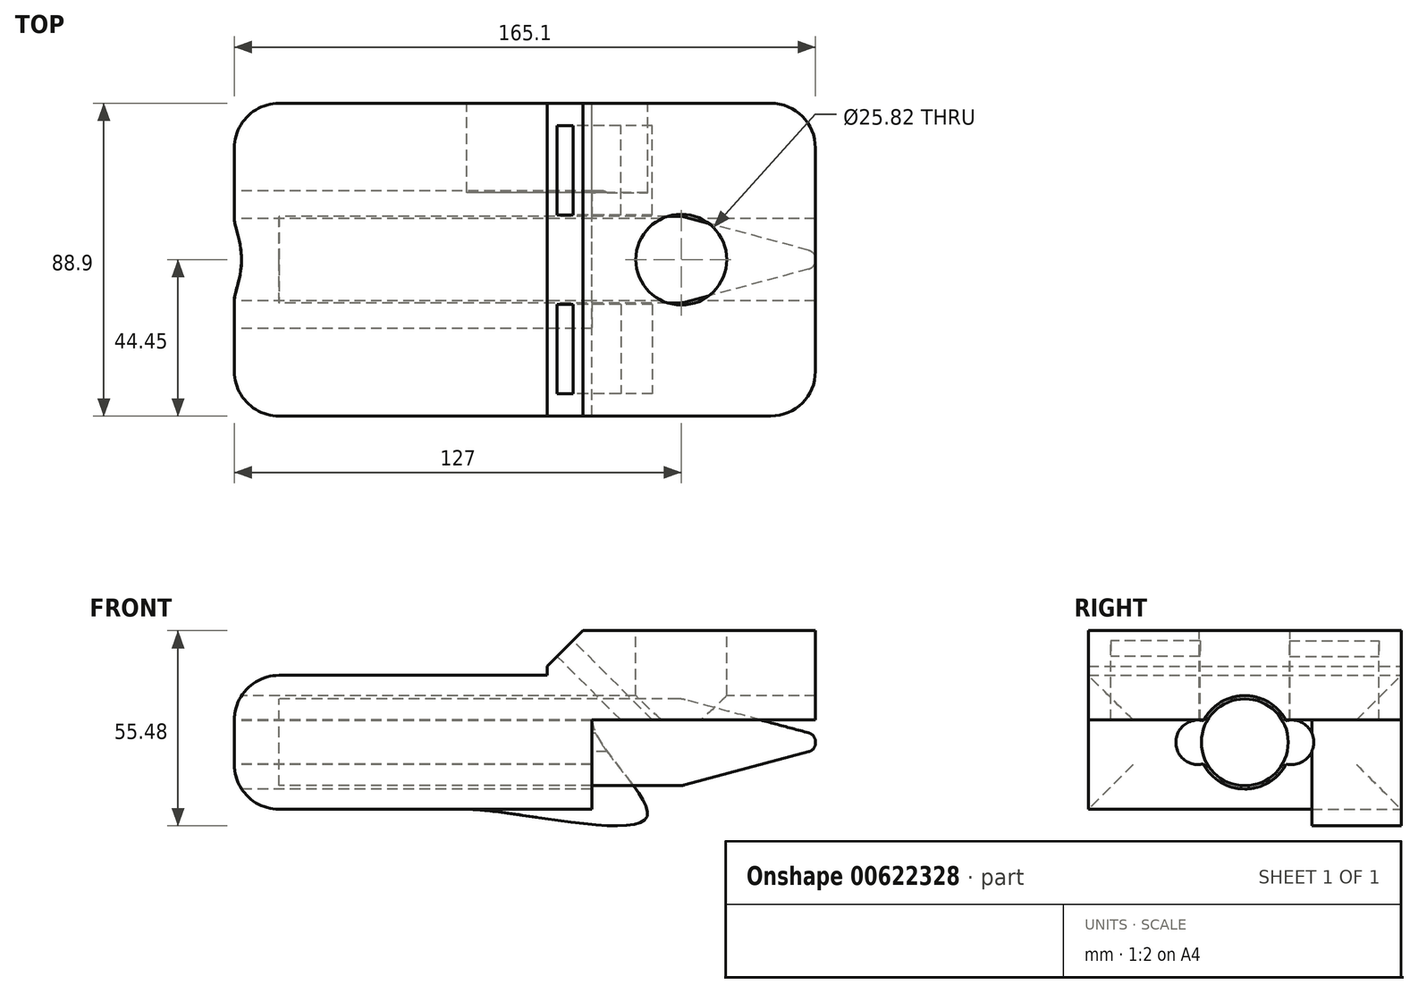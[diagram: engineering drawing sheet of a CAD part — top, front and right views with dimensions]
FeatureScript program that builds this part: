
annotation { "Feature Type Name" : "Feature", "Feature Type Description" : "" }
export const myFeature = defineFeature(function(context is Context, id is Id, definition is map)
    precondition{}
    {
        {
            var Q0;
            Q0=qCreatedBy(makeId("Front.planeOp"),FACE);
            var sketch = newSketch(context, id + "F0", { "sketchPlane" : qUnion([Q0])});
            skLineSegment(sketch, "E0.bottom", {"start": v(50.8, 19.05) * mm, "end": v(-50.8, 19.05) * mm});
            skLineSegment(sketch, "E0.top", {"start": v(50.8, -19.05) * mm, "end": v(-50.8, -19.05) * mm});
            skLineSegment(sketch, "E0.left", {"start": v(50.8, 19.05) * mm, "end": v(50.8, -19.05) * mm});
            skLineSegment(sketch, "E0.right", {"start": v(-50.8, 19.05) * mm, "end": v(-50.8, -19.05) * mm});
            skPoint(sketch, "E0.middle", {"position": v(0, 0) * mm});
            skLineSegment(sketch, "E1.bottom", {"start": v(38.1, 6.35) * mm, "end": v(114.3, 6.35) * mm});
            skLineSegment(sketch, "E1.top", {"start": v(38.1, 31.75) * mm, "end": v(114.3, 31.75) * mm});
            skLineSegment(sketch, "E1.left", {"start": v(38.1, 6.35) * mm, "end": v(38.1, 31.75) * mm});
            skLineSegment(sketch, "E1.right", {"start": v(114.3, 6.35) * mm, "end": v(114.3, 31.75) * mm});
            skPoint(sketch, "E1.middle", {"position": v(76.2, 19.05) * mm});
            skSolve(sketch);
        }
        {
            var Q0;
            Q0 = qSketchRegion(id + "F0", true);
            extrude(context, id + "F1", {"entities" : qUnion([Q0]), "depth" : 88.9 * mm, "offsetDistance" : 25.4 * mm});
        }
        {
            var Q0;
            Q0=makeQuery(id+"F1.opExtrude","SWEPT_FACE",FACE,{"disambiguationData":[OSD([sQuery(id+"F0.wireOp",EDGE,"E1.top")])]});
            var sketch = newSketch(context, id + "F2", { "sketchPlane" : qUnion([Q0])});
            skCircle(sketch, "E2", {"center": v(76.2, -44.45) * mm, "radius": 12.9 * mm});
            skPoint(sketch, "E2.centerSnap0", {"position": v(38.1, -44.45) * mm});
            skPoint(sketch, "E2.centerSnap1", {"position": v(76.2, -88.9) * mm});
            skSolve(sketch);
        }
        {
            var Q0;
            Q0 = qSketchRegion(id + "F2", true);
            extrude(context, id + "F3", {"entities" : qUnion([Q0]), "operationType" : NewBodyOperationType.REMOVE, "oppositeDirection" : true, "depth" : 25.4 * mm, "offsetDistance" : 25.4 * mm});
        }
        {
            var Q0;
            Q0=makeQuery(id+"F1.opExtrude","CAP_EDGE",EDGE,{"disambiguationData":[OSD([sQuery(id+"F0.wireOp",EDGE,"E1.right")])],"isStart":false});
            var Q1;
            Q1=makeQuery(id+"F1.opExtrude","CAP_EDGE",EDGE,{"disambiguationData":[OSD([sQuery(id+"F0.wireOp",EDGE,"E1.right")])],"isStart":true});
            var Q2;
            Q2=makeQuery(id+"F1.opExtrude","SWEPT_FACE",FACE,{"disambiguationData":[OSD([sQuery(id+"F0.wireOp",EDGE,"E0.right")])]});
            fillet(context, id + "F4", {"entities" : qUnion([Q0, Q1, Q2]), "radius" : 12.7 * mm, "tangentPropagation" : true, "allowEdgeOverflow" : false});
        }
        {
            var Q0;
            Q0=makeQuery(id+"F1.opExtrude","CAP_FACE",FACE,{"disambiguationData":[OSD([sQuery(id+"F0.wireOp",EDGE,"E0.bottom"),sQuery(id+"F0.wireOp",EDGE,"E0.top"),sQuery(id+"F0.wireOp",EDGE,"E0.left"),sQuery(id+"F0.wireOp",EDGE,"E0.right"),sQuery(id+"F0.wireOp",EDGE,"E1.bottom"),sQuery(id+"F0.wireOp",EDGE,"E1.top"),sQuery(id+"F0.wireOp",EDGE,"E1.left"),sQuery(id+"F0.wireOp",EDGE,"E1.right")])],"isStart":true});
            var sketch = newSketch(context, id + "F5", { "sketchPlane" : qUnion([Q0])});
            skFitSpline(sketch, "E3", {"points": [v(-50.8, 6.35) * mm, v(-66.41, -21.25) * mm, v(-15.28, -19.05) * mm], "startDerivative": vector(0, -51.15) * mm, "endDerivative": vector(68.34, 0) * mm});
            skLineSegment(sketch, "E4", {"start": v(-50.8, 6.35) * mm, "end": v(-50.8, -19.05) * mm});
            skLineSegment(sketch, "E5", {"start": v(-50.8, -19.05) * mm, "end": v(-15.28, -19.05) * mm});
            skSolve(sketch);
        }
        {
            var Q0;
            Q0 = qSketchRegion(id + "F5", true);
            extrude(context, id + "F6", {"entities" : qUnion([Q0]), "oppositeDirection" : true, "depth" : 25.4 * mm, "offsetDistance" : 25.4 * mm});
        }
        {
            var Q0;
            Q0=makeQuery(id+"F1.opExtrude","SWEPT_FACE",FACE,{"disambiguationData":[OSD([sQuery(id+"F0.wireOp",EDGE,"E0.right")])]});
            var sketch = newSketch(context, id + "F7", { "sketchPlane" : qUnion([Q0])});
            skLineSegment(sketch, "E6", {"start": v(12.7, 0) * mm, "end": v(76.2, 0) * mm});
            skCircle(sketch, "E7", {"center": v(44.45, 0) * mm, "radius": 13.26 * mm});
            skCircle(sketch, "E8", {"center": v(57.7, 0) * mm, "radius": 6.33 * mm});
            skCircle(sketch, "E9", {"center": v(31.2, 0) * mm, "radius": 6.35 * mm});
            skSolve(sketch);
        }
        {
            var Q0;
            Q0 = qSketchRegion(id + "F7", true);
            extrude(context, id + "F8", {"entities" : qUnion([Q0]), "operationType" : NewBodyOperationType.REMOVE, "endBound" : BoundingType.THROUGH_ALL, "oppositeDirection" : true, "depth" : 25.4 * mm, "offsetDistance" : 25.4 * mm});
        }
        {
            var Q0;
            {var subQ0=sQuery(id+"F0.wireOp",EDGE,"E0.bottom");Q0=makeQuery(id+"F4.opFillet","BLEND_EDGE",EDGE,{"blendedFrom":[makeQuery(id+"F1.opExtrude","SWEPT_EDGE",EDGE,{"disambiguationData":[OSD([subQ0,sQuery(id+"F0.wireOp",EDGE,"E0.right")])]}),makeQuery(id+"F1.opExtrude","SWEPT_FACE",FACE,{"disambiguationData":[OSD([subQ0])]})],"blendedInto":[makeQuery(id+"F1.opExtrude","SWEPT_FACE",FACE,{"disambiguationData":[OSD([subQ0])]})]});}
            cPlane(context, id + "F9", {"entities" : qUnion([Q0]), "cplaneType" : CPlaneType.LINE_ANGLE, "offset" : 25.4 * mm, "angle" : 90 * degree, "width" : 152.4 * mm, "height" : 152.4 * mm});
        }
        {
            var Q0;
            Q0=qCreatedBy(id+"F9.planeOp",FACE);
            var sketch = newSketch(context, id + "F10", { "sketchPlane" : qUnion([Q0])});
            skCircle(sketch, "E10", {"center": v(-44.44, 0) * mm, "radius": 12.35 * mm});
            skSolve(sketch);
        }
        {
            var Q0;
            Q0 = qSketchRegion(id + "F10", true);
            extrude(context, id + "F11", {"entities" : qUnion([Q0]), "operationType" : NewBodyOperationType.ADD, "depth" : 152.4 * mm, "offsetDistance" : 25.4 * mm});
        }
        {
            var Q0;
            Q0=makeQuery(id+"F11.opExtrude","CAP_EDGE",EDGE,{"disambiguationData":[OSD([sQuery(id+"F10.wireOp",EDGE,"E10")])],"isStart":false});
            chamfer(context, id + "F12", {"entities" : qUnion([Q0]), "chamferType" : ChamferType.OFFSET_ANGLE, "width" : 10.16 * mm, "oppositeDirection" : false, "angle" : 75 * degree, "tangentPropagation" : true});
        }
        {
            var Q0;
            {var subQ0=sQuery(id+"F10.wireOp",EDGE,"E10");Q0=makeQuery(id+"F12.opChamfer","BLEND_EDGE",EDGE,{"blendedFrom":[makeQuery(id+"F11.opExtrude","CAP_EDGE",EDGE,{"disambiguationData":[OSD([subQ0])],"isStart":false}),makeQuery(id+"F11.opExtrude","SWEPT_FACE",FACE,{"disambiguationData":[OSD([subQ0])]})],"blendedInto":[makeQuery(id+"F11.opExtrude","SWEPT_FACE",FACE,{"disambiguationData":[OSD([subQ0])]})]});}
            fillet(context, id + "F13", {"entities" : qUnion([Q0]), "radius" : 7.62 * mm, "tangentPropagation" : true, "allowEdgeOverflow" : false});
        }
        {
            var Q0;
            {var subQ0=sQuery(id+"F10.wireOp",EDGE,"E10");Q0=makeQuery(id+"F12.opChamfer","BLEND_EDGE",EDGE,{"blendedFrom":[makeQuery(id+"F11.opExtrude","CAP_EDGE",EDGE,{"disambiguationData":[OSD([subQ0])],"isStart":false}),makeQuery(id+"F11.opExtrude","CAP_FACE",FACE,{"disambiguationData":[OSD([subQ0])],"isStart":false})],"blendedInto":[makeQuery(id+"F11.opExtrude","CAP_FACE",FACE,{"disambiguationData":[OSD([subQ0])],"isStart":false})]});}
            fillet(context, id + "F14", {"entities" : qUnion([Q0]), "radius" : 2.54 * mm, "tangentPropagation" : true, "allowEdgeOverflow" : false});
        }
        {
            var Q0;
            Q0=makeQuery(id+"F1.opExtrude","SWEPT_EDGE",EDGE,{"disambiguationData":[OSD([sQuery(id+"F0.wireOp",EDGE,"E1.top"),sQuery(id+"F0.wireOp",EDGE,"E1.left")])]});
            chamfer(context, id + "F15", {"entities" : qUnion([Q0]), "width" : 10.16 * mm, "tangentPropagation" : true});
        }
        {
            var Q0;
            Q0=makeQuery(id+"F15.opChamfer","BLEND_FACE",FACE,{"disambiguationData":[OSD([sQuery(id+"F0.wireOp",EDGE,"E1.top"),sQuery(id+"F0.wireOp",EDGE,"E1.left")])]});
            var sketch = newSketch(context, id + "F16", { "sketchPlane" : qUnion([Q0])});
            skLineSegment(sketch, "E11.bottom", {"start": v(31.75, 52.57) * mm, "end": v(6.35, 52.57) * mm});
            skLineSegment(sketch, "E11.top", {"start": v(31.75, 46.22) * mm, "end": v(6.35, 46.22) * mm});
            skLineSegment(sketch, "E11.left", {"start": v(31.75, 52.57) * mm, "end": v(31.75, 46.22) * mm});
            skLineSegment(sketch, "E11.right", {"start": v(6.35, 52.57) * mm, "end": v(6.35, 46.22) * mm});
            skPoint(sketch, "E11.middle", {"position": v(19.05, 49.4) * mm});
            skPoint(sketch, "E11.middle.positionSnap0", {"position": v(0, 49.4) * mm});
            skPoint(sketch, "E11.centerSnap0", {"position": v(0, 49.4) * mm});
            skLineSegment(sketch, "E12.bottom", {"start": v(57.15, 52.57) * mm, "end": v(82.55, 52.57) * mm});
            skLineSegment(sketch, "E12.top", {"start": v(57.15, 46.22) * mm, "end": v(82.55, 46.22) * mm});
            skLineSegment(sketch, "E12.left", {"start": v(57.15, 52.57) * mm, "end": v(57.15, 46.22) * mm});
            skLineSegment(sketch, "E12.right", {"start": v(82.55, 52.57) * mm, "end": v(82.55, 46.22) * mm});
            skPoint(sketch, "E12.middle", {"position": v(69.85, 49.4) * mm});
            skPoint(sketch, "E12.middle.positionSnap0", {"position": v(88.9, 49.4) * mm});
            skPoint(sketch, "E12.centerSnap0", {"position": v(88.9, 49.4) * mm});
            skSolve(sketch);
        }
        {
            var Q0;
            Q0 = qSketchRegion(id + "F16", true);
            extrude(context, id + "F17", {"entities" : qUnion([Q0]), "operationType" : NewBodyOperationType.REMOVE, "endBound" : BoundingType.THROUGH_ALL, "oppositeDirection" : true, "depth" : 25.4 * mm, "offsetDistance" : 25.4 * mm});
        }
    });
